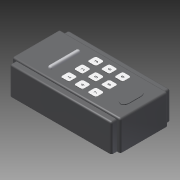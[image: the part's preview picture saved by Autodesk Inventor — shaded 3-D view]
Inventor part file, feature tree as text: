
AUTODESK INVENTOR PART (.ipt)
format: ipt  version: 2014 SP1 (Build 180222100, 222)  size: 701,952 bytes
history: native  units: in
note: dims shown in document units (in); Inventor stores cm internally (conversion verified against a paired STEP export)
features: fillet x7, sketch x7, extrude x6, shell x1, emboss x1
ambient origin geometry x8: Origin, YZ Plane, XZ Plane, XY Plane, X Axis, Y Axis, Z Axis, Center Point
bodies: Solid1 (feature_tree)
feature tree (22):
  extrude  "Extrusion1"  Depth=2.63in
  extrude  "Extrusion2"  Depth=4.543in
  extrude  "Extrusion3"  Depth=0.1515in
  extrude  "Extrusion4"  Depth=0.1515in
  fillet  "Fillet1"  Radius=0.1515in
  fillet  "Fillet2"  Radius=1.245in
  fillet  "Fillet3"  Radius=0.25in
  fillet  "Fillet4"  Radius=0.377in
  fillet  "Fillet5"  Radius=0.377in
  shell  "Shell1"  Thickness=0.2765in
  extrude  "Extrusion5"  Depth=0.075in TaperAngle=0.0deg
  fillet  "Fillet6"  Radius=0.075in
  extrude  "Extrusion6"  Depth=0.075in
  fillet  "Fillet7"  Radius=0.075in
  emboss  "Emboss1"
  sketch  "Sketch1"  dims[d0=4.8457in d1=2.63in]
  sketch  "Sketch2"  dims[d2=1.3257in d3=0.0in d4=4.543in]
  sketch  "Sketch3"  dims[d5=1.245in d6=0.1515in]
  sketch  "Sketch4"  dims[d7=0.25in d8=0.0in d9=0.1515in d10=0.1515in d11=1.245in d12=0.25in d13=0.0in d14=0.377in d15=0.377in]
  sketch  "Sketch5"  dims[d16=1.1811in d18=0.6in d19=1.1811in d21=0.6in d24=0.2765in]
  sketch  "Sketch6"  dims[d25=1.376in d26=0.03in d27=0.0in d28=0.075in]
  sketch  "Sketch7"  dims[d29=0.075in d30=0.075in d31=0.075in d32=0.075in d33=0.139in d35=1.364in d36=0.276in d37=0.5in d38=0.1in d39=0.0in d40=0.075in d41=0.415in d42=0.982in d43=0.499in d44=0.03in d45=0.0in d46=0.3in d47=0.01in d48=0.0in]
